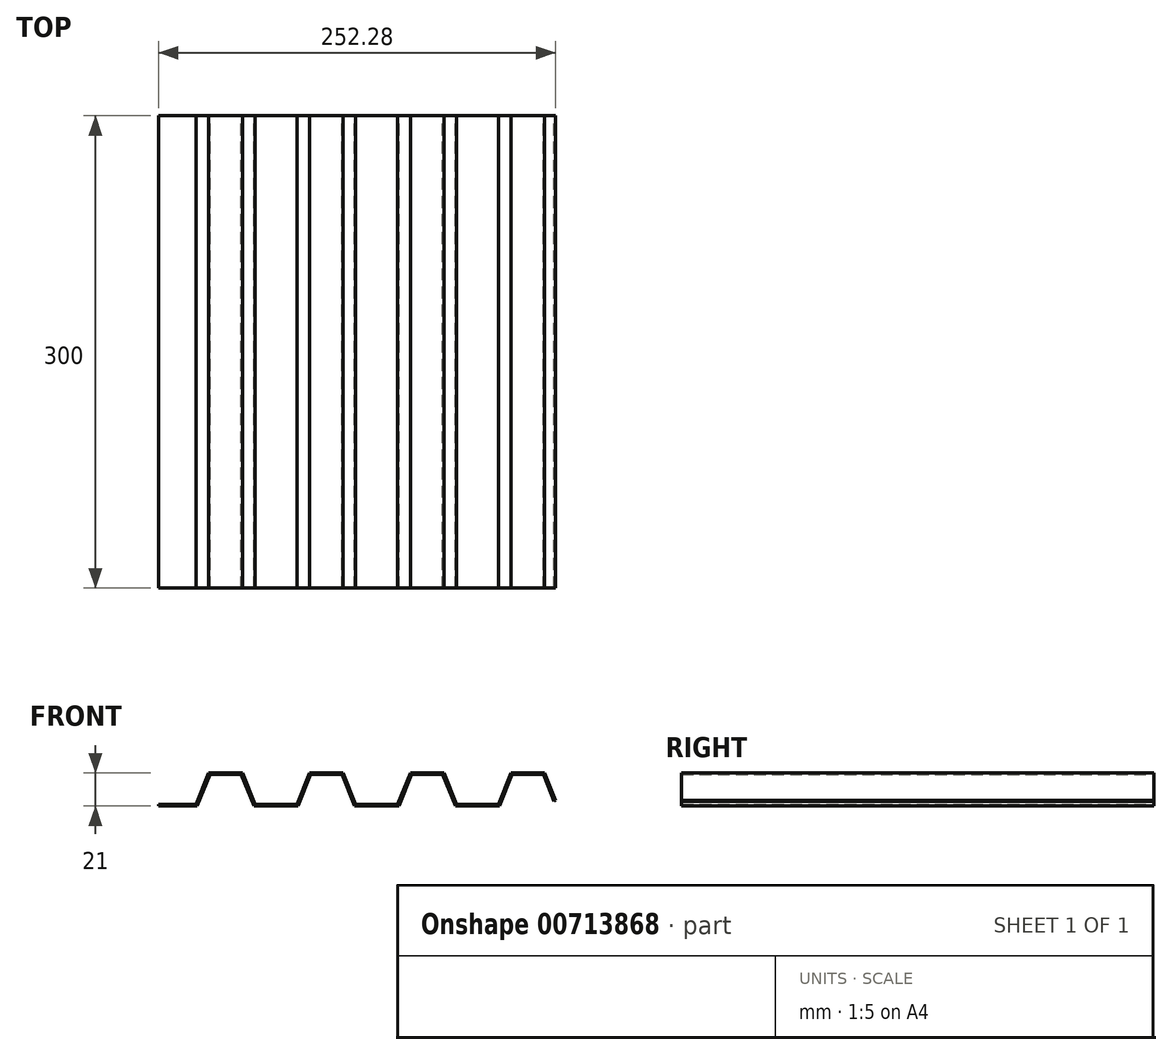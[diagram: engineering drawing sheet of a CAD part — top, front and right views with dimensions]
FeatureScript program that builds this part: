
annotation { "Feature Type Name" : "Feature", "Feature Type Description" : "" }
export const myFeature = defineFeature(function(context is Context, id is Id, definition is map)
    precondition{}
    {
        {
            var Q0;
            Q0=qCreatedBy(makeId("Front.planeOp"),FACE);
            var sketch = newSketch(context, id + "F0", { "sketchPlane" : qUnion([Q0])});
            skLineSegment(sketch, "E0", {"start": v(-75.05, -4) * mm, "end": v(-51.05, -4) * mm});
            skLineSegment(sketch, "E1", {"start": v(-51.05, -4) * mm, "end": v(-43.05, 16) * mm});
            skLineSegment(sketch, "E2", {"start": v(-43.05, 16) * mm, "end": v(-21.76, 16) * mm});
            skLineSegment(sketch, "E3", {"start": v(-21.76, 16) * mm, "end": v(-13.76, -4) * mm});
            skLineSegment(sketch, "E4", {"start": v(-13.76, -4) * mm, "end": v(12.95, -4) * mm});
            skLineSegment(sketch, "E5", {"start": v(12.95, -4) * mm, "end": v(20.95, 16) * mm});
            skLineSegment(sketch, "E6", {"start": v(20.95, 16) * mm, "end": v(42.24, 16) * mm});
            skLineSegment(sketch, "E7", {"start": v(42.24, 16) * mm, "end": v(50.24, -4) * mm});
            skLineSegment(sketch, "E8", {"start": v(50.24, -4) * mm, "end": v(76.95, -4) * mm});
            skLineSegment(sketch, "E9", {"start": v(76.95, -4) * mm, "end": v(84.95, 16) * mm});
            skLineSegment(sketch, "E10", {"start": v(84.95, 16) * mm, "end": v(106.24, 16) * mm});
            skLineSegment(sketch, "E11", {"start": v(106.24, 16) * mm, "end": v(114.24, -4) * mm});
            skLineSegment(sketch, "E12", {"start": v(114.24, -4) * mm, "end": v(140.95, -4) * mm});
            skLineSegment(sketch, "E13", {"start": v(140.95, -4) * mm, "end": v(148.95, 16) * mm});
            skLineSegment(sketch, "E14", {"start": v(148.95, 16) * mm, "end": v(170.24, 16) * mm});
            skLineSegment(sketch, "E15", {"start": v(170.24, 16) * mm, "end": v(177.23, -1.49) * mm});
            skLineSegment(sketch, "E16.0", {"start": v(169.56, 15) * mm, "end": v(176.3, -1.86) * mm});
            skLineSegment(sketch, "E16.1", {"start": v(149.62, 15) * mm, "end": v(169.56, 15) * mm});
            skLineSegment(sketch, "E16.2", {"start": v(141.62, -5) * mm, "end": v(149.62, 15) * mm});
            skLineSegment(sketch, "E16.3", {"start": v(113.56, -5) * mm, "end": v(141.62, -5) * mm});
            skLineSegment(sketch, "E16.4", {"start": v(105.56, 15) * mm, "end": v(113.56, -5) * mm});
            skLineSegment(sketch, "E16.5", {"start": v(85.62, 15) * mm, "end": v(105.56, 15) * mm});
            skLineSegment(sketch, "E16.6", {"start": v(-22.44, 15) * mm, "end": v(-14.44, -5) * mm});
            skLineSegment(sketch, "E16.7", {"start": v(-42.38, 15) * mm, "end": v(-22.44, 15) * mm});
            skLineSegment(sketch, "E16.8", {"start": v(-50.38, -5) * mm, "end": v(-42.38, 15) * mm});
            skLineSegment(sketch, "E16.9", {"start": v(-75.05, -5) * mm, "end": v(-50.38, -5) * mm});
            skLineSegment(sketch, "E16.10", {"start": v(-14.44, -5) * mm, "end": v(13.62, -5) * mm});
            skLineSegment(sketch, "E16.11", {"start": v(13.62, -5) * mm, "end": v(21.62, 15) * mm});
            skLineSegment(sketch, "E16.12", {"start": v(21.62, 15) * mm, "end": v(41.56, 15) * mm});
            skLineSegment(sketch, "E16.13", {"start": v(41.56, 15) * mm, "end": v(49.56, -5) * mm});
            skLineSegment(sketch, "E16.14", {"start": v(49.56, -5) * mm, "end": v(77.62, -5) * mm});
            skLineSegment(sketch, "E16.15", {"start": v(77.62, -5) * mm, "end": v(85.62, 15) * mm});
            skLineSegment(sketch, "E17", {"start": v(-75.05, -4) * mm, "end": v(-75.05, -5) * mm});
            skLineSegment(sketch, "E18", {"start": v(177.23, -1.49) * mm, "end": v(176.3, -1.86) * mm});
            skSolve(sketch);
        }
        {
            var Q0;
            Q0=qSketchRegion(id+"F0",true);
            extrude(context, id + "F1", {"entities" : qUnion([Q0]), "depth" : 300 * mm});
        }
    });
